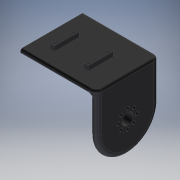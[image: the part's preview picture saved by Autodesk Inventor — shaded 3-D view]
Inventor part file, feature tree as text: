
AUTODESK INVENTOR PART (.ipt)
format: ipt  version: 2018 (Build 220112000, 112)  size: 264,192 bytes
history: native  units: mm
features: sketch x5, extrude x4, fillet x4, projected_geometry x2, hole x1
ambient origin geometry x8: Origin, YZ Plane, XZ Plane, XY Plane, X Axis, Y Axis, Z Axis, Center Point
bodies: Solid1 (feature_tree)
feature tree (16):
  extrude  "Extrusion1"  Depth=10.0mm
  extrude  "Extrusion2"  Depth=5.0mm TaperAngle=0.0deg
  extrude  "Extrusion3"  Depth=2.0mm TaperAngle=0.0deg
  fillet  "Fillet1"  Radius=2.0mm
  extrude  "Extrusion6"  Depth=4.0mm
  hole  "Hole2"  [1 undecoded]
  fillet  "Fillet2"  Radius=4.0mm
  fillet  "Fillet3"  Radius=5.0mm
  fillet  "Fillet4"  Radius=2.0mm
  sketch  "Sketch1"  dims[d1=80.0mm d2=1.0mm d3=10.0mm d4=16.0mm d5=2.9mm d6=360.0deg d7=14.5mm d8=0.0mm d9=56.0mm]
  sketch  "Sketch2"  dims[d10=34.0mm d11=5.0mm d12=0.0mm]
  sketch  "Sketch3"  dims[d13=4.0mm d14=61.5mm d15=0.0mm d16=2.0mm]
  projected_geometry  "Projected Loop1"
  sketch  "Sketch4"  dims[d34=4.0mm d35=22.0mm]
  sketch  "Sketch7"  dims[d36=4.0mm d37=22.0mm d38=4.0mm d39=0.0mm d40=2.4mm d41=6.0mm d42=4.0mm d43=2.0mm d44=90.0deg d45=2.0mm d46=20.594885mm d47=5.0mm d48=2.0mm d49=2.0mm]
  projected_geometry  "Projected Loop8"
note: 1 required parameter value undecoded (feature->parameter linkage not recoverable at this tier; creation-order binding heuristic only, values carry confidence <= 0.55)
